# Revit family: Hutprofil
name_source: partatom
category: HLS-Bauteile
revit_build: Autodesk Revit 2017 (Build: 20190507_1515(x64)
units: mm (PartAtom-declared; Revit-internal decimal feet)

## family parameters
Arbeitsebenenbasiert = Ja
Beim Laden mit Abzugskörper schneiden = Nein
Bemaßung runder Anschluss = Durchmesser verwenden
Gemeinsam genutzt = Ja
Immer vertikal = Nein
Raumberechnungspunkt = Nein
Teiletyp = Normal

## types (8) — shared parameters
Anschlusslochung = 13 mm
Breite Material = 35 mm
Fabrikat = MEFA
Firma = MEFA Befestigungs- und Montagesysteme GmbH
Langloch = 13 x 17,5 mm
Lochabstand = 105 mm
Länge = 135 mm
Material = Stahl
Materialname = S235
Mengeneinheit = St
Oberflaeche = galvanisch verzinkt
Stärke Material = 4 mm  [stored 0.0131234 ft]
Vorgabe-Ansicht = 1219 mm
max. zul. Last = 3.50 kN

## per-type parameters (varying)
| type | Artikelnummer | Gewicht | Gewicht pro Bauteil | H | Höhe | Kurztext1 | Kurztext2 | Länge Innen | Profiltyp | vpe |
| Hutprofil  26 | 08162326 | 0.18 kg | 0.18 kg | 26 mm | 26 mm | Hutprofil C-Profil 45/26 | Höhe 26 mm Langloch 13 x 17,5 mm | 46 mm | 45/26 | 25 St |
| Hutprofil  45 | 08162445 | 0.22 kg | 0.22 kg | 45 mm  [stored 0.147638 ft] | 45 mm | Hutprofil C-Profil 45/45 | Höhe 45 mm Langloch 13 x 17,5 mm | 46 mm | 45/45 | 25 St |
| Hutprofil  52 | 08162452 | 0.24 kg | 0.24 kg | 52 mm | 52 mm | Hutprofil Doppel-C-Profil 45/52 | Höhe 52 mm Langloch 13 x 17,5 mm | 46 mm | 45/52 | 25 St |
| Hutprofil  60 | 0816253 | 0.25 kg | 0.25 kg | 60 mm  [stored 0.19685 ft] | 60 mm | Hutprofil C-Profil 45/60 | Höhe 60 mm Langloch 13 x 17,5 mm | 46 mm | 45/60 | 25 St |
| Hutprofil  75 | 08162875 | 0.29 kg | 0.29 kg | 75 mm | 75 mm | Hutprofil C-Profil 45/75 | Höhe 75 mm Langloch 13 x 17,5 mm | 61 mm | 45/75 | 25 St |
| Hutprofil  90 | 08162690 | 0.32 kg | 0.32 kg | 90 mm  [stored 0.295276 ft] | 90 mm | Hutprofil Doppel-C-Profil 45/90 | Höhe 90 mm Langloch 13 x 17,5 mm | 46 mm | 45/90 | 25 St |
| Hutprofil 120 | 0816274 | 0.39 kg | 0.39 kg | 120 mm  [stored 0.393701 ft] | 120 mm | Hutprofil Doppel-C-Profil 45/120 | Höhe 120 mm Langloch 13 x 17,5 mm | 46 mm | 45/120 | 25 St |
| Hutprofil 150 | 081628150 | 0.45 kg | 0.45 kg | 150 mm | 150 mm | Hutprofil Doppel-C-Profil 45/150 | Höhe 150 mm Langloch 13 x 17,5 mm | 46 mm | 45/150 | 1 St |

note: [stored X ft] marks values corroborated as IEEE doubles in the binary element streams (Revit-internal decimal feet)
